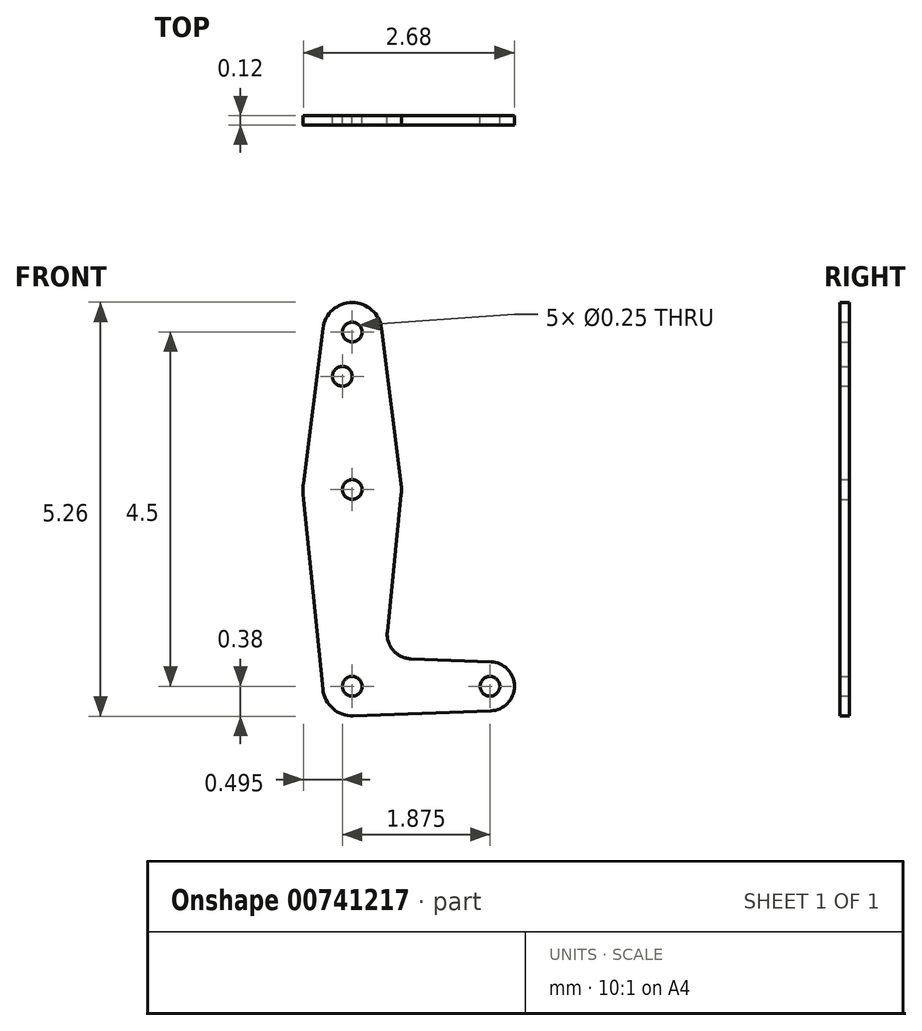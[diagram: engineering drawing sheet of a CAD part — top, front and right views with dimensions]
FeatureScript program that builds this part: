
annotation { "Feature Type Name" : "Feature", "Feature Type Description" : "" }
export const myFeature = defineFeature(function(context is Context, id is Id, definition is map)
    precondition{}
    {
        {
            var Q0;
            Q0=qCreatedBy(makeId("Front.planeOp"),FACE);
            var sketch = newSketch(context, id + "F0", { "sketchPlane" : qUnion([Q0])});
            skLineSegment(sketch, "E0", {"start": v(0, 4.5) * mm, "end": v(0, 0) * mm, "construction": true});
            skLineSegment(sketch, "E1", {"start": v(0, 0) * mm, "end": v(1.75, 0) * mm, "construction": true});
            skCircle(sketch, "E2", {"center": v(0, 0) * mm, "radius": 0.38 * mm});
            skCircle(sketch, "E3", {"center": v(0, 4.5) * mm, "radius": 0.38 * mm});
            skCircle(sketch, "E4", {"center": v(0, 2.5) * mm, "radius": 0.62 * mm});
            skCircle(sketch, "E5", {"center": v(1.75, 0) * mm, "radius": 0.31 * mm});
            skLineSegment(sketch, "E6", {"start": v(-0.37, 4.55) * mm, "end": v(-0.62, 2.58) * mm});
            skLineSegment(sketch, "E7", {"start": v(-0.62, 2.44) * mm, "end": v(-0.37, -0.04) * mm});
            skLineSegment(sketch, "E8", {"start": v(0.45, 0.7) * mm, "end": v(0.62, 2.44) * mm});
            skLineSegment(sketch, "E9", {"start": v(0.62, 2.58) * mm, "end": v(0.37, 4.55) * mm});
            skLineSegment(sketch, "E10", {"start": v(0.75, 0.35) * mm, "end": v(1.76, 0.31) * mm});
            skLineSegment(sketch, "E11", {"start": v(0.01, -0.37) * mm, "end": v(1.76, -0.31) * mm});
            skCircle(sketch, "E12", {"center": v(-0.12, 3.94) * mm, "radius": 0.12 * mm});
            skCircle(sketch, "E13", {"center": v(0, 4.5) * mm, "radius": 0.12 * mm});
            skCircle(sketch, "E14", {"center": v(0, 2.5) * mm, "radius": 0.12 * mm});
            skCircle(sketch, "E15", {"center": v(0, 0) * mm, "radius": 0.12 * mm});
            skCircle(sketch, "E16", {"center": v(1.75, 0) * mm, "radius": 0.12 * mm});
            skArc(sketch, "E17.filletArc", {"start": v(0.45, 0.7) * mm, "mid": v(0.52, 0.46) * mm, "end": v(0.75, 0.35) * mm});
            skSolve(sketch);
        }
        {
            var Q0;
            Q0 = qSketchRegion(id + "F0", true);
            extrude(context, id + "F1", {"entities" : qUnion([Q0]), "depth" : 0.12 * mm, "offsetDistance" : 25 * mm});
        }
    });
